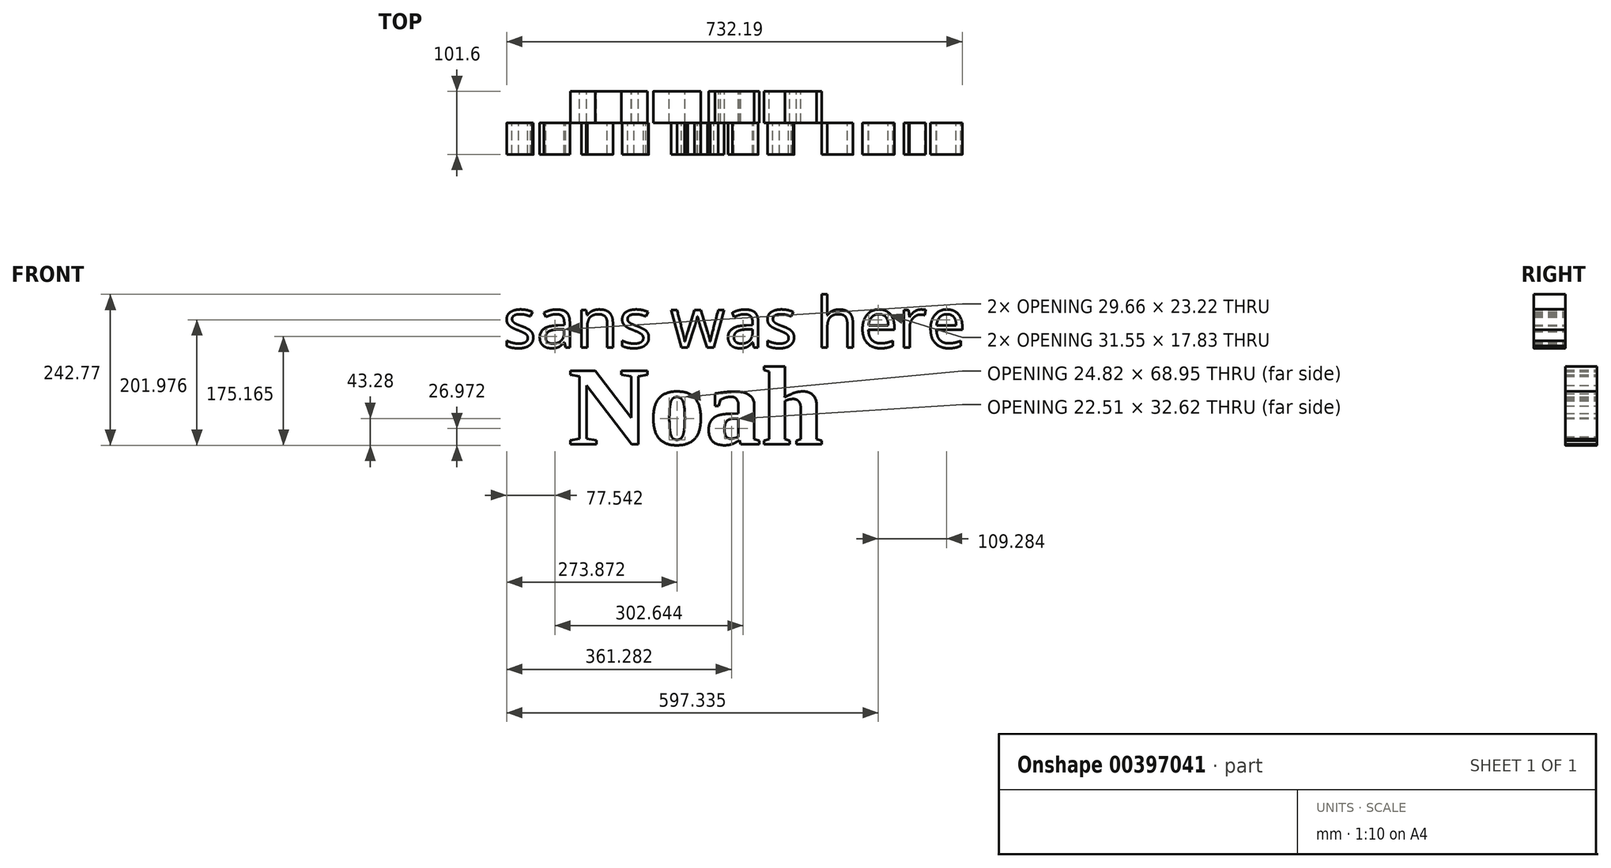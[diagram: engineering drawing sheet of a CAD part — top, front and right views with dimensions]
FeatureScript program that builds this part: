
annotation { "Feature Type Name" : "Feature", "Feature Type Description" : "" }
export const myFeature = defineFeature(function(context is Context, id is Id, definition is map)
    precondition{}
    {
        {
            var Q0;
            Q0=qCreatedBy(makeId("Front.planeOp"),FACE);
            var sketch = newSketch(context, id + "F0", { "sketchPlane" : qUnion([Q0])});
            skText(sketch, "E0", { "text": "Noah", "fontName": "Tinos-Bold.ttf"});
            const initialGuessF0  = {"E0": [-0.1979, -0.06368, 1, 0, 0.12968]};
            skSetInitialGuess(sketch, initialGuessF0);
            skSolve(sketch);
        }
        {
            var Q0;
            Q0 = qSketchRegion(id + "F0", true);
            extrude(context, id + "F1", {"entities" : qUnion([Q0]), "depth" : 50.8 * mm});
        }
        {
            var Q0;
            Q0=makeQuery(id+"F1.opExtrude","CAP_FACE",FACE,{"disambiguationData":[OSD([sQuery(id+"F0.wireOp",EDGE,"E0.sketch_text.stroke-0"),sQuery(id+"F0.wireOp",EDGE,"E0.sketch_text.stroke-1"),sQuery(id+"F0.wireOp",EDGE,"E0.sketch_text.stroke-2"),sQuery(id+"F0.wireOp",EDGE,"E0.sketch_text.stroke-3"),sQuery(id+"F0.wireOp",EDGE,"E0.sketch_text.stroke-4"),sQuery(id+"F0.wireOp",EDGE,"E0.sketch_text.stroke-5"),sQuery(id+"F0.wireOp",EDGE,"E0.sketch_text.stroke-6"),sQuery(id+"F0.wireOp",EDGE,"E0.sketch_text.stroke-7"),sQuery(id+"F0.wireOp",EDGE,"E0.sketch_text.stroke-8"),sQuery(id+"F0.wireOp",EDGE,"E0.sketch_text.stroke-9"),sQuery(id+"F0.wireOp",EDGE,"E0.sketch_text.stroke-10"),sQuery(id+"F0.wireOp",EDGE,"E0.sketch_text.stroke-11"),sQuery(id+"F0.wireOp",EDGE,"E0.sketch_text.stroke-12"),sQuery(id+"F0.wireOp",EDGE,"E0.sketch_text.stroke-13"),sQuery(id+"F0.wireOp",EDGE,"E0.sketch_text.stroke-14"),sQuery(id+"F0.wireOp",EDGE,"E0.sketch_text.stroke-15"),sQuery(id+"F0.wireOp",EDGE,"E0.sketch_text.stroke-16"),sQuery(id+"F0.wireOp",EDGE,"E0.sketch_text.stroke-17"),sQuery(id+"F0.wireOp",EDGE,"E0.sketch_text.stroke-18"),sQuery(id+"F0.wireOp",EDGE,"E0.sketch_text.stroke-19")])],"isStart":false});
            var sketch = newSketch(context, id + "F2", { "sketchPlane" : qUnion([Q0])});
            skText(sketch, "E1", { "text": "sans was here\n", "fontName": "OpenSans-Regular.ttf"});
            const initialGuessF2  = {"E1": [-0.3025, 0.09166, 1, 0, 0.08117]};
            skSetInitialGuess(sketch, initialGuessF2);
            skSolve(sketch);
        }
        {
            var Q0;
            Q0 = qSketchRegion(id + "F2", true);
            extrude(context, id + "F3", {"entities" : qUnion([Q0]), "depth" : 50.8 * mm});
        }
    });
